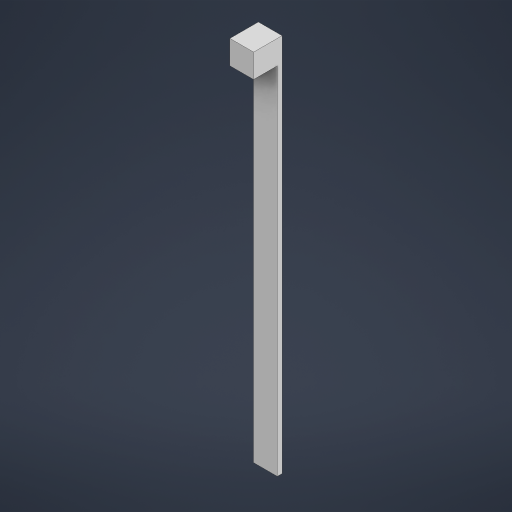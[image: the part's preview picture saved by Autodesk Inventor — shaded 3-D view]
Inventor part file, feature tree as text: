
AUTODESK INVENTOR PART (.ipt)
format: ipt  version: 2024.2 (Build 282272000, 272)  size: 418,304 bytes
history: native  units: mm
features: extrude x2, sketch x2, other x1
ambient origin geometry x8: Origin, YZ Plane, XZ Plane, XY Plane, X Axis, Y Axis, Z Axis, Center Point
bodies: Body1 (feature_tree)
feature tree (5):
  other  "솔리드1"
  extrude  "돌출1"  Depth=5.0mm
  extrude  "돌출2"  Depth=80.0mm
  sketch  "스케치1"
  sketch  "스케치2"
